# Revit family: Cypher-C1
name_source: partatom
category: Lighting Fixtures
units: mm (PartAtom-declared; Revit-internal decimal feet)

## family parameters
Always vertical = Yes
Cut with Voids When Loaded = No
Host = Wall
Light Source = Yes
OmniClass Number = 23.80.70.11.14
OmniClass Title = General Luminaries, Directional
Part Type = Normal
Room Calculation Point = No
Round Connector Dimension = Use Diameter
Shared = No

## types (6) — shared parameters
120 Voltage = Yes
277 Voltage = No
Assembly Code = D5020
Box Finish = White
Color Filter = 16777215
Description = Cypher allows designers to mix and match optics for best-in-class aesthetics and performance
Dimming Lamp Color Temperature Shift = <None>
Emit Shape Visible in Rendering = No
Emit from Rectangle Length = 2 "
Emit from Rectangle Width = 4 "
Glass = White Glass
Lamp = 360° Light Distribution
Load Classification = Lighting
Manufacturer = Architectural Area Lighting
Model = Cypher - Accent Scale
Photometric Notes = For more Photometric files please refer to the website
Power Factor = 1
Tilt Angle = 90.00°
URL = https://www.currentlighting.com
Voltage = 120 V
zero-valued in all types: Default Elevation

## per-type parameters (varying)
| type | Apparent Load | Photometric Web File | Wattage Comments | Watts |
| CY1-15-3K7-1-1D-R | 17 VA | CY1-15-3K7-1-1D-R.IES | 15W, 1500 nominal lumens | 17 W |
| CY1-15-4K7-1-WG-R | 17 VA | CY1-15-4K7-1-WG-R.IES | 15W, 1500 nominal lumens | 17 W |
| CY1-15-5K7-1-3D-R | 17 VA | CY1-15-5K7-1-3D-R.IES | 15W, 1500 nominal lumens | 17 W |
| CY1-25-3K7-1-1-R | 26 VA | CY1-25-3K7-1-1-R.IES | 25W, 2500 nominal lumens | 26 W |
| CY1-25-4K7-1-4-R | 26 VA | CY1-25-4K7-1-4-R.IES | 25W, 2500 nominal lumens | 26 W |
| CY1-25-5K7-1-SP-R | 26 VA | CY1-25-5K7-1-SP-R.IES | 25W, 2500 nominal lumens | 26 W |

## geometry (parser evidence)
native form markers: Blend x32, Sweep x4
no freeform markers — native parametric forms only
